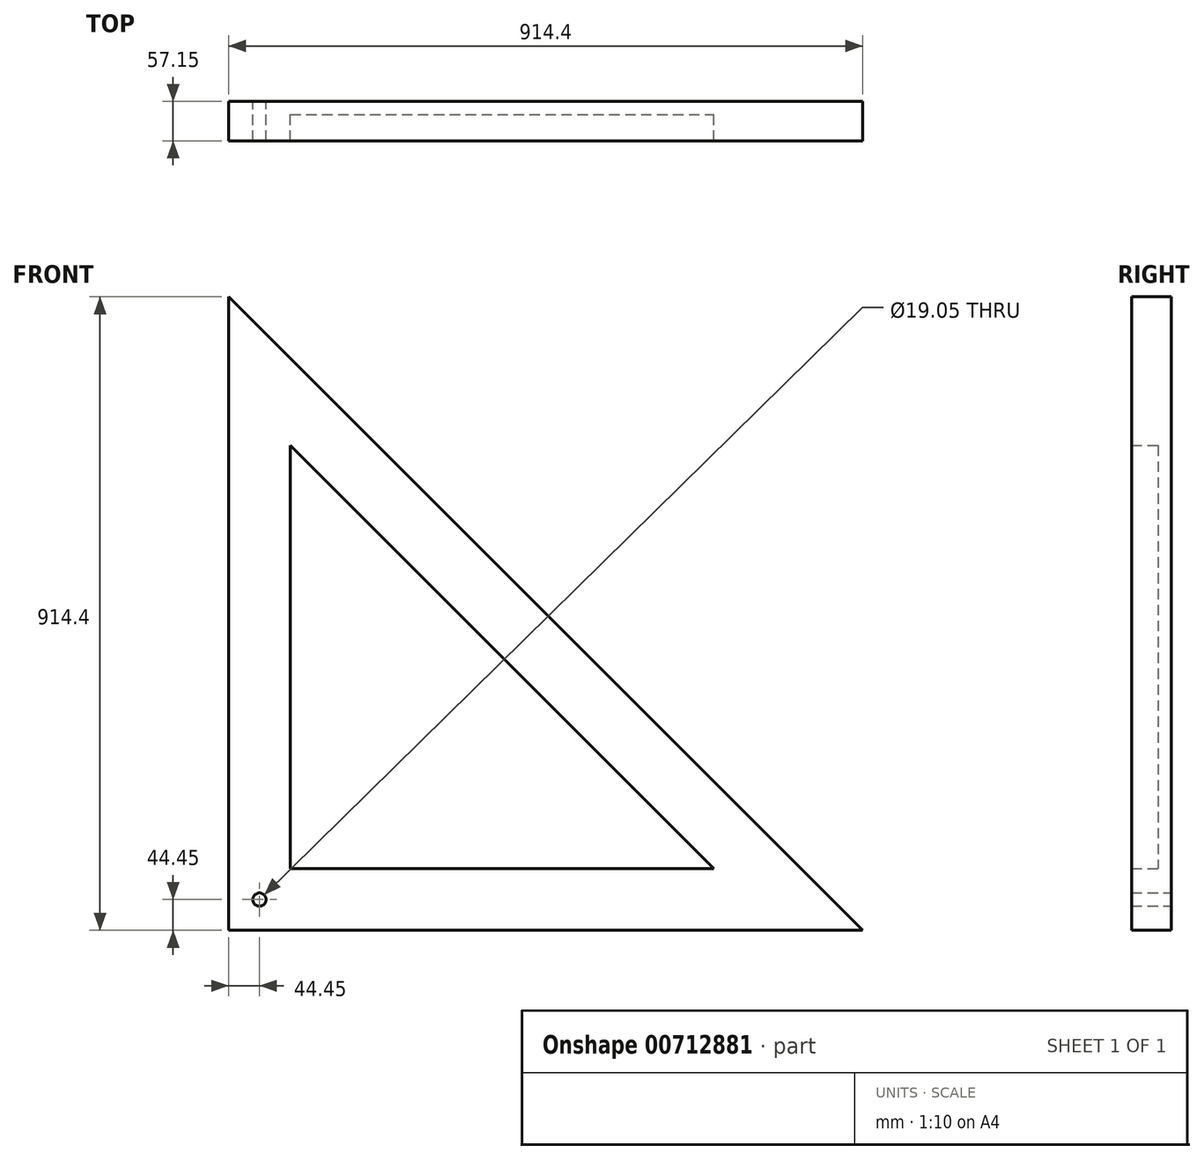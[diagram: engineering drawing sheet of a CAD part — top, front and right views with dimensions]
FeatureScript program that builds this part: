
annotation { "Feature Type Name" : "Feature", "Feature Type Description" : "" }
export const myFeature = defineFeature(function(context is Context, id is Id, definition is map)
    precondition{}
    {
        {
            var Q0;
            Q0=qCreatedBy(makeId("Front.planeOp"),FACE);
            var sketch = newSketch(context, id + "F0", { "sketchPlane" : qUnion([Q0])});
            skLineSegment(sketch, "E0", {"start": v(0, 914.4) * mm, "end": v(914.4, 0) * mm});
            skLineSegment(sketch, "E1", {"start": v(914.4, 0) * mm, "end": v(914.4, 0) * mm});
            skLineSegment(sketch, "E2", {"start": v(0, 0) * mm, "end": v(0, 0) * mm});
            skLineSegment(sketch, "E3", {"start": v(0, 0) * mm, "end": v(914.4, 0) * mm});
            skLineSegment(sketch, "E4", {"start": v(0, 914.4) * mm, "end": v(0, 0) * mm});
            skCircle(sketch, "E5", {"center": v(44.45, 44.45) * mm, "radius": 9.52 * mm});
            skLineSegment(sketch, "E6.0", {"start": v(88.9, 88.9) * mm, "end": v(699.78, 88.9) * mm});
            skLineSegment(sketch, "E6.1", {"start": v(88.9, 699.78) * mm, "end": v(88.9, 88.9) * mm});
            skLineSegment(sketch, "E6.2", {"start": v(88.9, 699.78) * mm, "end": v(699.78, 88.9) * mm});
            skSolve(sketch);
        }
        {
            var Q0;
            Q0=makeQuery(id+"F0.imprint","IMPRINT",FACE,{"disambiguationData":[TD([[makeQuery(id+"F0.imprint","IMPRINT",EDGE,{"derivedFrom":sQuery(id+"F0.wireOp",EDGE,"E0")}),-1.0]])]});
            extrude(context, id + "F1", {"entities" : qUnion([Q0]), "depth" : 38.1 * mm, "offsetDistance" : 25.4 * mm});
        }
        {
            var Q0;
            Q0=makeQuery(id+"F0.imprint","IMPRINT",FACE,{"disambiguationData":[TD([[makeQuery(id+"F0.imprint","IMPRINT",EDGE,{"derivedFrom":sQuery(id+"F0.wireOp",EDGE,"E6.0")}),1.0]])]});
            var Q1;
            Q1=makeQuery(id+"F0.imprint","IMPRINT",FACE,{"disambiguationData":[TD([[makeQuery(id+"F0.imprint","IMPRINT",EDGE,{"derivedFrom":sQuery(id+"F0.wireOp",EDGE,"E0")}),-1.0]])]});
            extrude(context, id + "F2", {"entities" : qUnion([Q0, Q1]), "operationType" : NewBodyOperationType.ADD, "depth" : -19.05 * mm, "offsetDistance" : 25.4 * mm});
        }
    });
